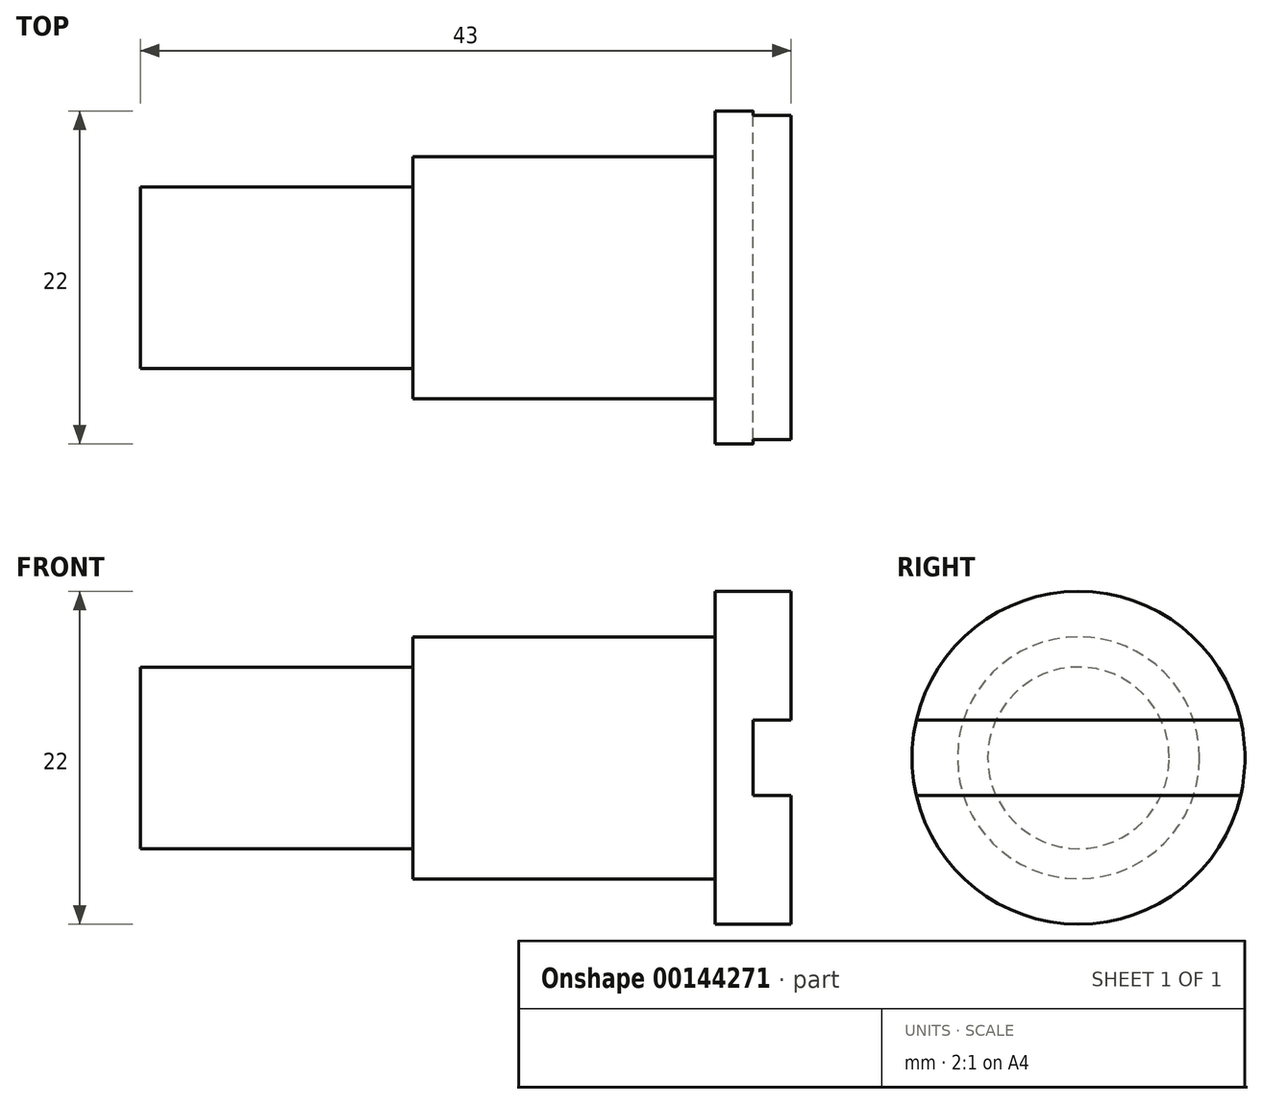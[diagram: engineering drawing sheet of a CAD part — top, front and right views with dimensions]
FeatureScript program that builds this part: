
annotation { "Feature Type Name" : "Feature", "Feature Type Description" : "" }
export const myFeature = defineFeature(function(context is Context, id is Id, definition is map)
    precondition{}
    {
        {
            var Q0;
            Q0=qCreatedBy(makeId("Front.planeOp"),FACE);
            var sketch = newSketch(context, id + "F0", { "sketchPlane" : qUnion([Q0])});
            skLineSegment(sketch, "E0", {"start": v(-62.56, 0) * mm, "end": v(41.68, 0) * mm, "construction": true});
            skLineSegment(sketch, "E1", {"start": v(-38, 0) * mm, "end": v(-38, 6) * mm});
            skLineSegment(sketch, "E2", {"start": v(-38, 6) * mm, "end": v(-20, 6) * mm});
            skLineSegment(sketch, "E3", {"start": v(-20, 6) * mm, "end": v(-20, 8) * mm});
            skLineSegment(sketch, "E4", {"start": v(-20, 8) * mm, "end": v(0, 8) * mm});
            skLineSegment(sketch, "E5", {"start": v(0, 8) * mm, "end": v(0, 11) * mm});
            skLineSegment(sketch, "E6", {"start": v(0, 11) * mm, "end": v(5, 11) * mm});
            skLineSegment(sketch, "E7", {"start": v(5, 11) * mm, "end": v(5, 0) * mm});
            skLineSegment(sketch, "E8", {"start": v(-38, 0) * mm, "end": v(5, 0) * mm});
            skSolve(sketch);
        }
        {
            var Q0;
            Q0 = qSketchRegion(id + "F0", true);
            var Q1;
            Q1=sQuery(id+"F0.wireOp",EDGE,"E0");
            revolve(context, id + "F1", {"entities" : qUnion([Q0]), "axis" : qUnion([Q1]), "revolveType" : RevolveType.FULL});
        }
        {
            var Q0;
            Q0=makeQuery(id+"F1.opRevolve","SWEPT_FACE",FACE,{"disambiguationData":[OSD([sQuery(id+"F0.wireOp",EDGE,"E7")])]});
            var sketch = newSketch(context, id + "F2", { "sketchPlane" : qUnion([Q0])});
            skLineSegment(sketch, "E9.bottom", {"start": v(-33.15, 2.5) * mm, "end": v(29.04, 2.5) * mm});
            skLineSegment(sketch, "E9.top", {"start": v(-33.15, -2.5) * mm, "end": v(29.04, -2.5) * mm});
            skLineSegment(sketch, "E9.left", {"start": v(-33.15, 2.5) * mm, "end": v(-33.15, -2.5) * mm});
            skLineSegment(sketch, "E9.right", {"start": v(29.04, 2.5) * mm, "end": v(29.04, -2.5) * mm});
            skSolve(sketch);
        }
        {
            var Q0;
            Q0 = qSketchRegion(id + "F2", true);
            extrude(context, id + "F3", {"entities" : qUnion([Q0]), "operationType" : NewBodyOperationType.REMOVE, "oppositeDirection" : true, "depth" : 2.5 * mm});
        }
    });
